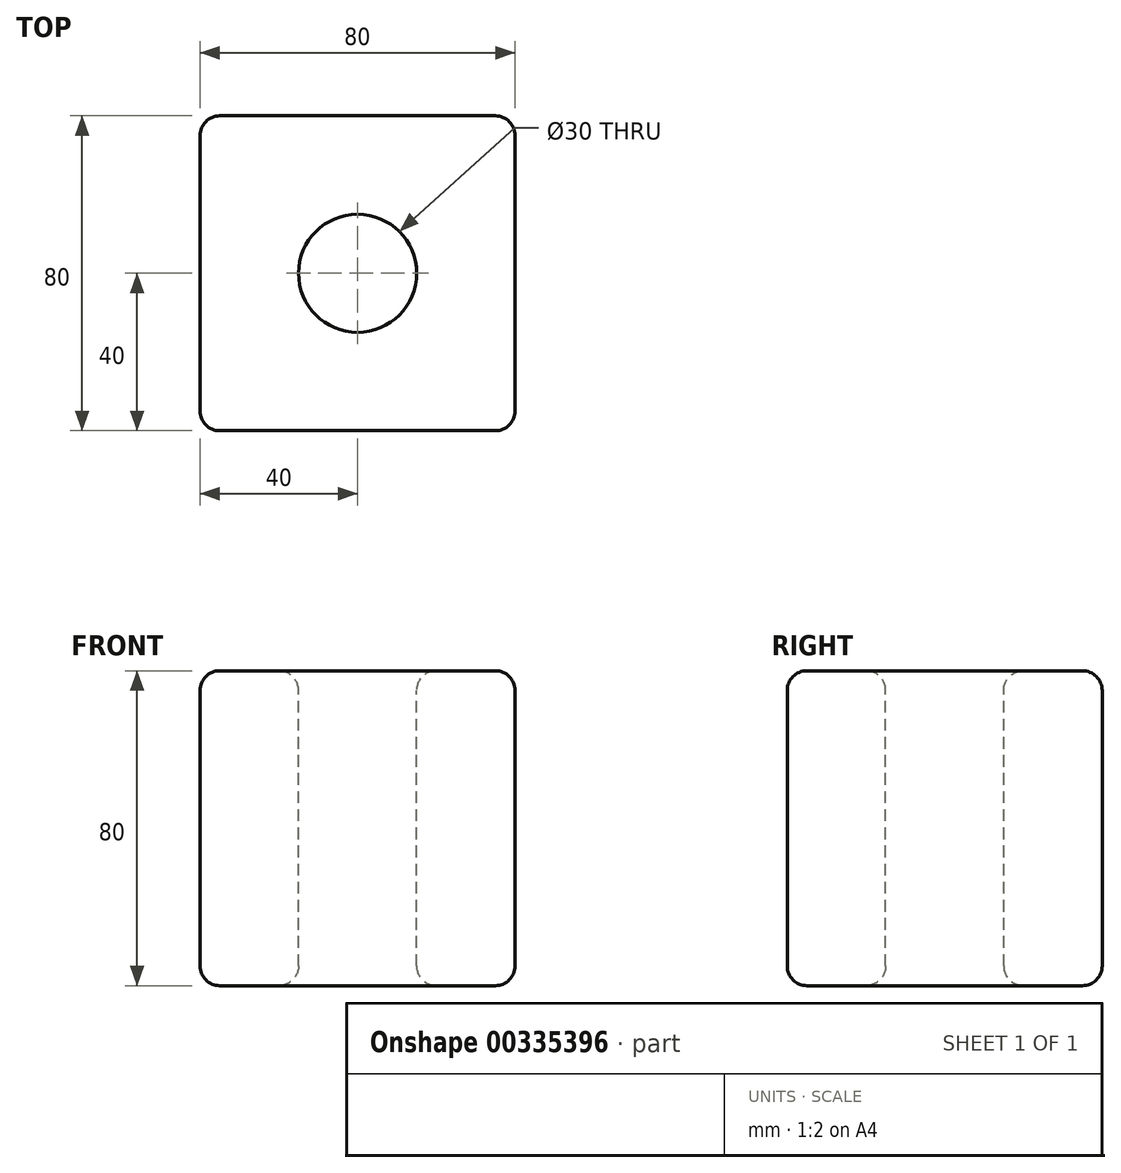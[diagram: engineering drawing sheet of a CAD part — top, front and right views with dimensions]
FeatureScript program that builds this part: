
annotation { "Feature Type Name" : "Feature", "Feature Type Description" : "" }
export const myFeature = defineFeature(function(context is Context, id is Id, definition is map)
    precondition{}
    {
        {
            var Q0;
            Q0=qCreatedBy(makeId("Top.planeOp"),FACE);
            var sketch = newSketch(context, id + "F0", { "sketchPlane" : qUnion([Q0])});
            skLineSegment(sketch, "E0.bottom", {"start": v(40, -40) * mm, "end": v(-40, -40) * mm});
            skLineSegment(sketch, "E0.top", {"start": v(40, 40) * mm, "end": v(-40, 40) * mm});
            skLineSegment(sketch, "E0.left", {"start": v(40, -40) * mm, "end": v(40, 40) * mm});
            skLineSegment(sketch, "E0.right", {"start": v(-40, -40) * mm, "end": v(-40, 40) * mm});
            skPoint(sketch, "E0.middle", {"position": v(0, 0) * mm});
            skSolve(sketch);
        }
        {
            var Q0;
            Q0=makeQuery(id+"F0.imprint","IMPRINT",FACE,{"disambiguationData":[TD([[makeQuery(id+"F0.imprint","IMPRINT",EDGE,{"derivedFrom":sQuery(id+"F0.wireOp",EDGE,"E0.bottom")}),-1.0]])]});
            extrude(context, id + "F1", {"entities" : qUnion([Q0]), "endBound" : BoundingType.SYMMETRIC, "depth" : 80 * mm});
        }
        {
            var Q0;
            Q0=makeQuery(id+"F1.opExtrude","CAP_EDGE",EDGE,{"disambiguationData":[OSD([sQuery(id+"F0.wireOp",EDGE,"E0.top")])],"isStart":false});
            var Q1;
            Q1=makeQuery(id+"F1.opExtrude","CAP_EDGE",EDGE,{"disambiguationData":[OSD([sQuery(id+"F0.wireOp",EDGE,"E0.right")])],"isStart":false});
            var Q2;
            Q2=makeQuery(id+"F1.opExtrude","CAP_EDGE",EDGE,{"disambiguationData":[OSD([sQuery(id+"F0.wireOp",EDGE,"E0.left")])],"isStart":false});
            var Q3;
            Q3=makeQuery(id+"F1.opExtrude","CAP_EDGE",EDGE,{"disambiguationData":[OSD([sQuery(id+"F0.wireOp",EDGE,"E0.bottom")])],"isStart":false});
            var Q4;
            Q4=makeQuery(id+"F1.opExtrude","SWEPT_EDGE",EDGE,{"disambiguationData":[OSD([sQuery(id+"F0.wireOp",EDGE,"E0.top"),sQuery(id+"F0.wireOp",EDGE,"E0.right")])]});
            var Q5;
            Q5=makeQuery(id+"F1.opExtrude","CAP_EDGE",EDGE,{"disambiguationData":[OSD([sQuery(id+"F0.wireOp",EDGE,"E0.right")])],"isStart":true});
            var Q6;
            Q6=makeQuery(id+"F1.opExtrude","SWEPT_EDGE",EDGE,{"disambiguationData":[OSD([sQuery(id+"F0.wireOp",EDGE,"E0.bottom"),sQuery(id+"F0.wireOp",EDGE,"E0.right")])]});
            var Q7;
            Q7=makeQuery(id+"F1.opExtrude","CAP_EDGE",EDGE,{"disambiguationData":[OSD([sQuery(id+"F0.wireOp",EDGE,"E0.top")])],"isStart":true});
            var Q8;
            Q8=makeQuery(id+"F1.opExtrude","CAP_EDGE",EDGE,{"disambiguationData":[OSD([sQuery(id+"F0.wireOp",EDGE,"E0.left")])],"isStart":true});
            var Q9;
            Q9=makeQuery(id+"F1.opExtrude","CAP_EDGE",EDGE,{"disambiguationData":[OSD([sQuery(id+"F0.wireOp",EDGE,"E0.bottom")])],"isStart":true});
            var Q10;
            Q10=makeQuery(id+"F1.opExtrude","SWEPT_EDGE",EDGE,{"disambiguationData":[OSD([sQuery(id+"F0.wireOp",EDGE,"E0.top"),sQuery(id+"F0.wireOp",EDGE,"E0.left")])]});
            var Q11;
            Q11=makeQuery(id+"F1.opExtrude","SWEPT_EDGE",EDGE,{"disambiguationData":[OSD([sQuery(id+"F0.wireOp",EDGE,"E0.bottom"),sQuery(id+"F0.wireOp",EDGE,"E0.left")])]});
            fillet(context, id + "F2", {"entities" : qUnion([Q0, Q1, Q2, Q3, Q4, Q5, Q6, Q7, Q8, Q9, Q10, Q11]), "radius" : 5 * mm, "tangentPropagation" : true, "allowEdgeOverflow" : false});
        }
        {
            var Q0;
            Q0=makeQuery(id+"F1.opExtrude","CAP_FACE",FACE,{"disambiguationData":[OSD([sQuery(id+"F0.wireOp",EDGE,"E0.bottom"),sQuery(id+"F0.wireOp",EDGE,"E0.top"),sQuery(id+"F0.wireOp",EDGE,"E0.left"),sQuery(id+"F0.wireOp",EDGE,"E0.right")])],"isStart":false});
            var sketch = newSketch(context, id + "F3", { "sketchPlane" : qUnion([Q0])});
            skCircle(sketch, "E1", {"center": v(0, 0) * mm, "radius": 15 * mm});
            skSolve(sketch);
        }
        {
            var Q0;
            Q0=makeQuery(id+"F3.imprint","IMPRINT",FACE,{"disambiguationData":[TD([[makeQuery(id+"F3.imprint","IMPRINT",EDGE,{"derivedFrom":sQuery(id+"F3.wireOp",EDGE,"E1")}),1.0]])]});
            extrude(context, id + "F4", {"entities" : qUnion([Q0]), "operationType" : NewBodyOperationType.REMOVE, "endBound" : BoundingType.THROUGH_ALL, "oppositeDirection" : true, "depth" : 25 * mm});
        }
        {
            var Q0;
            Q0=makeQuery(id+"F4.boolean.opBoolean","COPY",FACE,{"derivedFrom":makeQuery(id+"F4.opExtrude","SWEPT_FACE",FACE,{"disambiguationData":[OSD([sQuery(id+"F3.wireOp",EDGE,"E1")])]})});
            var Q1;
            Q1=makeQuery(id+"F4.boolean.opBoolean","COPY",EDGE,{"derivedFrom":makeQuery(id+"F4.opExtrude","CAP_EDGE",EDGE,{"disambiguationData":[OSD([sQuery(id+"F3.wireOp",EDGE,"E1")])],"isStart":true})});
            var Q2;
            Q2=makeQuery(id+"F4.boolean.opBoolean","INTERSECT",EDGE,{"derivedFrom":[makeQuery(id+"F1.opExtrude","CAP_FACE",FACE,{"disambiguationData":[OSD([sQuery(id+"F0.wireOp",EDGE,"E0.bottom"),sQuery(id+"F0.wireOp",EDGE,"E0.top"),sQuery(id+"F0.wireOp",EDGE,"E0.left"),sQuery(id+"F0.wireOp",EDGE,"E0.right")])],"isStart":true}),makeQuery(id+"F4.opExtrude","SWEPT_FACE",FACE,{"disambiguationData":[OSD([sQuery(id+"F3.wireOp",EDGE,"E1")])]})]});
            fillet(context, id + "F5", {"entities" : qUnion([Q0, Q1, Q2]), "radius" : 5 * mm, "tangentPropagation" : true, "allowEdgeOverflow" : false});
        }
    });
